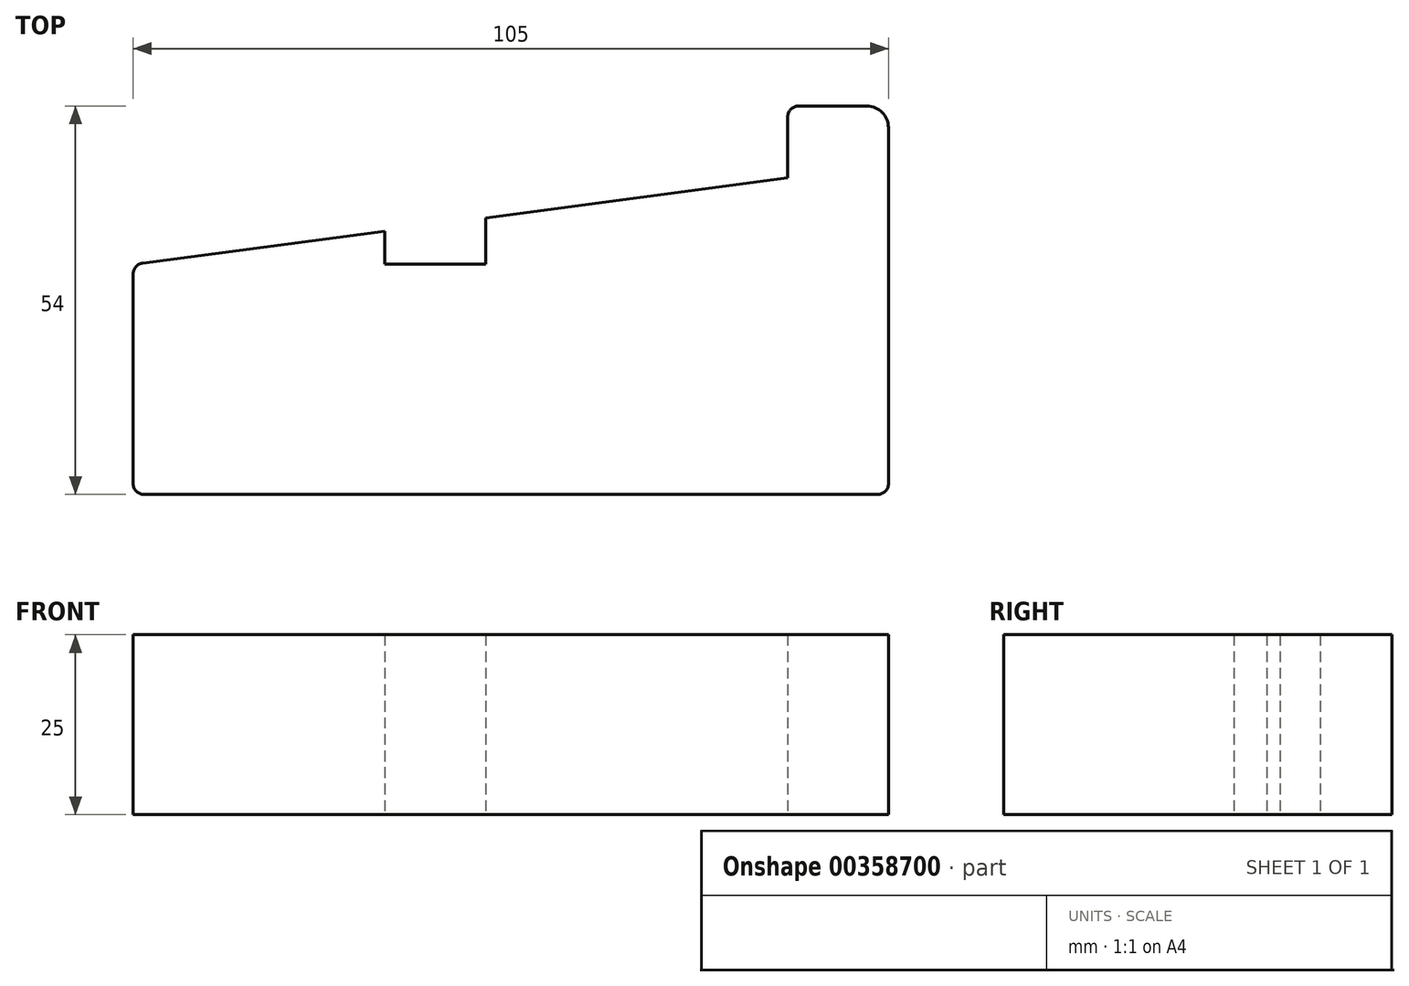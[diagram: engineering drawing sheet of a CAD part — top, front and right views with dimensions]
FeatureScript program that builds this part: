
annotation { "Feature Type Name" : "Feature", "Feature Type Description" : "" }
export const myFeature = defineFeature(function(context is Context, id is Id, definition is map)
    precondition{}
    {
        {
            var Q0;
            Q0=qCreatedBy(makeId("Top.planeOp"),FACE);
            var sketch = newSketch(context, id + "F0", { "sketchPlane" : qUnion([Q0])});
            skLineSegment(sketch, "E0", {"start": v(-51, -51.96) * mm, "end": v(51, -51.96) * mm});
            skLineSegment(sketch, "E1", {"start": v(52.5, -50.46) * mm, "end": v(52.5, -0.96) * mm});
            skLineSegment(sketch, "E2", {"start": v(49.5, 2.04) * mm, "end": v(40, 2.04) * mm});
            skLineSegment(sketch, "E3", {"start": v(38.5, 0.54) * mm, "end": v(38.5, -7.96) * mm});
            skLineSegment(sketch, "E4", {"start": v(-52.5, -50.46) * mm, "end": v(-52.5, -21.28) * mm});
            skLineSegment(sketch, "E5", {"start": v(38.5, -7.96) * mm, "end": v(-3.5, -13.5) * mm});
            skLineSegment(sketch, "E6", {"start": v(-17.5, -15.35) * mm, "end": v(-17.5, -19.96) * mm});
            skLineSegment(sketch, "E7", {"start": v(-17.5, -19.96) * mm, "end": v(-3.5, -19.96) * mm});
            skLineSegment(sketch, "E8", {"start": v(-3.5, -19.96) * mm, "end": v(-3.5, -13.5) * mm});
            skLineSegment(sketch, "E9.trimOffspring", {"start": v(-17.5, -15.35) * mm, "end": v(-51.2, -19.79) * mm});
            skPoint(sketch, "E10.end.orphan", {"position": v(-17.5, 3.93) * mm});
            skPoint(sketch, "E11.end.orphan", {"position": v(3.35, -19.96) * mm});
            skPoint(sketch, "E12.visualSharp", {"position": v(-52.5, -19.96) * mm});
            skArc(sketch, "E12.filletArc", {"start": v(-51.2, -19.79) * mm, "mid": v(-52.13, -20.29) * mm, "end": v(-52.5, -21.28) * mm});
            skPoint(sketch, "E13.visualSharp", {"position": v(-52.5, -51.96) * mm});
            skArc(sketch, "E13.filletArc", {"start": v(-52.5, -50.46) * mm, "mid": v(-52.06, -51.52) * mm, "end": v(-51, -51.96) * mm});
            skPoint(sketch, "E14.visualSharp", {"position": v(52.5, -51.96) * mm});
            skArc(sketch, "E14.filletArc", {"start": v(51, -51.96) * mm, "mid": v(52.06, -51.52) * mm, "end": v(52.5, -50.46) * mm});
            skPoint(sketch, "E15.visualSharp", {"position": v(38.5, 2.04) * mm});
            skArc(sketch, "E15.filletArc", {"start": v(40, 2.04) * mm, "mid": v(38.94, 1.6) * mm, "end": v(38.5, 0.54) * mm});
            skPoint(sketch, "E16.visualSharp", {"position": v(52.5, 2.04) * mm});
            skArc(sketch, "E16.filletArc", {"start": v(52.5, -0.96) * mm, "mid": v(51.62, 1.16) * mm, "end": v(49.5, 2.04) * mm});
            skSolve(sketch);
        }
        {
            var Q0;
            Q0=makeQuery(id+"F0.imprint","IMPRINT",FACE,{"disambiguationData":[TD([[makeQuery(id+"F0.imprint","IMPRINT",EDGE,{"derivedFrom":sQuery(id+"F0.wireOp",EDGE,"E0")}),1.0]])]});
            extrude(context, id + "F1", {"entities" : qUnion([Q0]), "depth" : 25 * mm});
        }
    });
